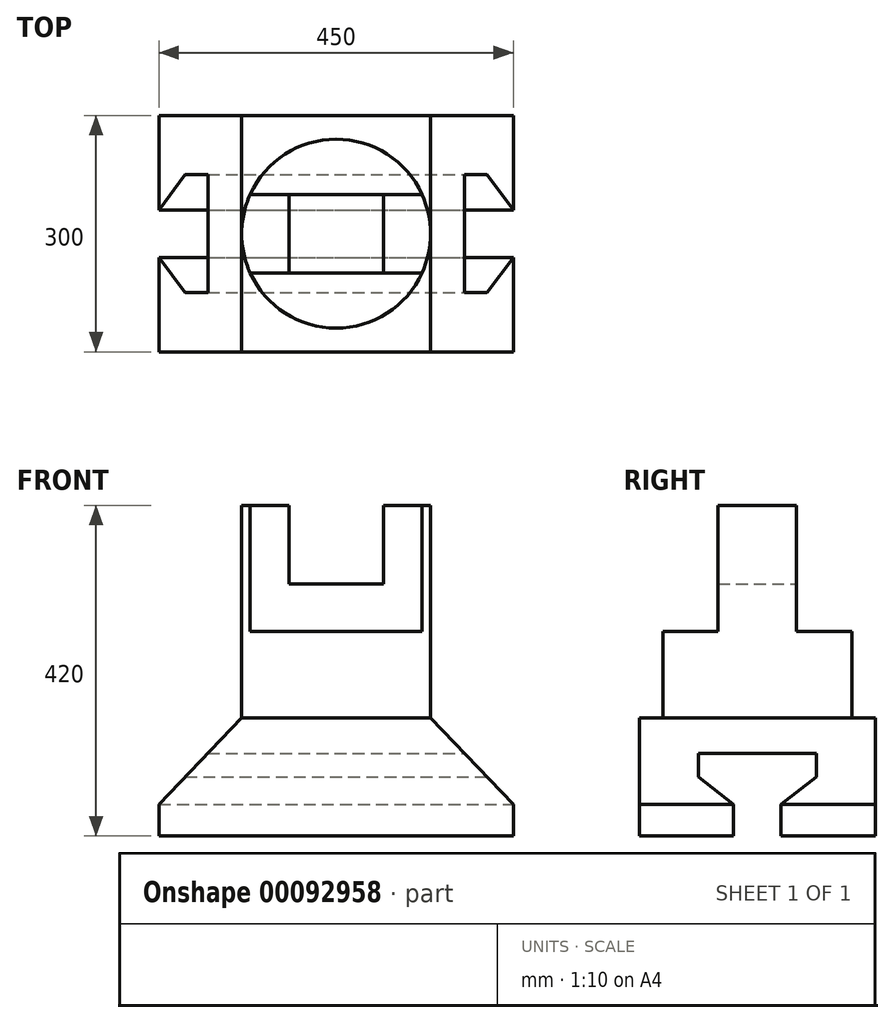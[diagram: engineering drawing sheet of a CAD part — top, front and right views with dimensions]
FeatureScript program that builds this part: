
annotation { "Feature Type Name" : "Feature", "Feature Type Description" : "" }
export const myFeature = defineFeature(function(context is Context, id is Id, definition is map)
    precondition{}
    {
        {
            var Q0;
            Q0=qCreatedBy(makeId("Front.planeOp"),FACE);
            var sketch = newSketch(context, id + "F0", { "sketchPlane" : qUnion([Q0])});
            skLineSegment(sketch, "E0.bottom", {"start": v(225, -75) * mm, "end": v(-225, -75) * mm});
            skLineSegment(sketch, "E0.top", {"start": v(120, 75) * mm, "end": v(-120, 75) * mm});
            skLineSegment(sketch, "E0.left", {"start": v(225, -75) * mm, "end": v(225, -35) * mm});
            skLineSegment(sketch, "E0.right", {"start": v(-225, -75) * mm, "end": v(-225, -35) * mm});
            skPoint(sketch, "E0.middle", {"position": v(0, 0) * mm});
            skLineSegment(sketch, "E1", {"start": v(-225, -35) * mm, "end": v(-120, 75) * mm});
            skLineSegment(sketch, "E2", {"start": v(120, 75) * mm, "end": v(225, -35) * mm});
            skPoint(sketch, "E3.orphan", {"position": v(-225, 75) * mm});
            skPoint(sketch, "E4.orphan", {"position": v(225, 75) * mm});
            skSolve(sketch);
        }
        {
            var Q0;
            Q0 = qSketchRegion(id + "F0", true);
            extrude(context, id + "F1", {"entities" : qUnion([Q0]), "endBound" : BoundingType.SYMMETRIC, "depth" : 300 * mm});
        }
        {
            var Q0;
            Q0=makeQuery(id+"F1.opExtrude","SWEPT_FACE",FACE,{"disambiguationData":[OSD([sQuery(id+"F0.wireOp",EDGE,"E0.top")])]});
            var sketch = newSketch(context, id + "F2", { "sketchPlane" : qUnion([Q0])});
            skCircle(sketch, "E5", {"center": v(0, 0) * mm, "radius": 120 * mm});
            skSolve(sketch);
        }
        {
            var Q0;
            Q0 = qSketchRegion(id + "F2", true);
            extrude(context, id + "F3", {"entities" : qUnion([Q0]), "operationType" : NewBodyOperationType.ADD, "depth" : 270 * mm});
        }
        {
            var Q0;
            Q0=makeQuery(id+"F3.opExtrude","CAP_FACE",FACE,{"disambiguationData":[OSD([sQuery(id+"F2.wireOp",EDGE,"E5")])],"isStart":false});
            var sketch = newSketch(context, id + "F4", { "sketchPlane" : qUnion([Q0])});
            skLineSegment(sketch, "E6.bottom", {"start": v(358.65, 50) * mm, "end": v(-358.65, 50) * mm});
            skLineSegment(sketch, "E6.top", {"start": v(358.65, -50) * mm, "end": v(-358.65, -50) * mm});
            skPoint(sketch, "E6.middle", {"position": v(0, 0) * mm});
            skLineSegment(sketch, "E7.bottom", {"start": v(-358.65, 50) * mm, "end": v(358.65, 50) * mm});
            skLineSegment(sketch, "E7.top", {"start": v(-358.65, 161.25) * mm, "end": v(358.65, 161.25) * mm});
            skLineSegment(sketch, "E7.left", {"start": v(-358.65, 50) * mm, "end": v(-358.65, 161.25) * mm});
            skLineSegment(sketch, "E7.right", {"start": v(358.65, 50) * mm, "end": v(358.65, 161.25) * mm});
            skLineSegment(sketch, "E8.bottom", {"start": v(358.65, -50) * mm, "end": v(-338.67, -50) * mm});
            skLineSegment(sketch, "E8.top", {"start": v(358.65, -198.35) * mm, "end": v(-338.67, -198.35) * mm});
            skLineSegment(sketch, "E8.left", {"start": v(358.65, -50) * mm, "end": v(358.65, -198.35) * mm});
            skLineSegment(sketch, "E8.right", {"start": v(-338.67, -50) * mm, "end": v(-338.67, -198.35) * mm});
            skSolve(sketch);
        }
        {
            var Q0;
            Q0 = qSketchRegion(id + "F4", true);
            extrude(context, id + "F5", {"entities" : qUnion([Q0]), "operationType" : NewBodyOperationType.REMOVE, "oppositeDirection" : true, "depth" : 160 * mm});
        }
        {
            var Q0;
            Q0=makeQuery(id+"F3.opExtrude","CAP_FACE",FACE,{"disambiguationData":[OSD([sQuery(id+"F2.wireOp",EDGE,"E5")])],"isStart":false});
            var sketch = newSketch(context, id + "F6", { "sketchPlane" : qUnion([Q0])});
            skLineSegment(sketch, "E9.bottom", {"start": v(60, -50) * mm, "end": v(-60, -50) * mm});
            skLineSegment(sketch, "E9.top", {"start": v(60, 50) * mm, "end": v(-60, 50) * mm});
            skLineSegment(sketch, "E9.left", {"start": v(60, -50) * mm, "end": v(60, 50) * mm});
            skLineSegment(sketch, "E9.right", {"start": v(-60, -50) * mm, "end": v(-60, 50) * mm});
            skPoint(sketch, "E9.middle", {"position": v(0, 0) * mm});
            skSolve(sketch);
        }
        {
            var Q0;
            Q0 = qSketchRegion(id + "F6", true);
            extrude(context, id + "F7", {"entities" : qUnion([Q0]), "operationType" : NewBodyOperationType.REMOVE, "oppositeDirection" : true, "depth" : 100 * mm});
        }
        {
            var Q0;
            Q0=makeQuery(id+"F1.opExtrude","SWEPT_FACE",FACE,{"disambiguationData":[OSD([sQuery(id+"F0.wireOp",EDGE,"E0.left")])]});
            var sketch = newSketch(context, id + "F8", { "sketchPlane" : qUnion([Q0])});
            skLineSegment(sketch, "E10", {"start": v(-30, -75) * mm, "end": v(-30, -35) * mm});
            skLineSegment(sketch, "E11", {"start": v(-30, -35) * mm, "end": v(-75, 0) * mm});
            skLineSegment(sketch, "E12", {"start": v(-75, 0) * mm, "end": v(-75, 30) * mm});
            skLineSegment(sketch, "E13", {"start": v(-75, 30) * mm, "end": v(75, 30) * mm});
            skLineSegment(sketch, "E14", {"start": v(75, 30) * mm, "end": v(75, 0) * mm});
            skLineSegment(sketch, "E15", {"start": v(75, 0) * mm, "end": v(30, -35) * mm});
            skLineSegment(sketch, "E16", {"start": v(30, -35) * mm, "end": v(30, -75) * mm});
            skLineSegment(sketch, "E17", {"start": v(30, -75) * mm, "end": v(-30, -75) * mm});
            skPoint(sketch, "E18", {"position": v(0, -75) * mm});
            skPoint(sketch, "E19", {"position": v(0, 30) * mm});
            skSolve(sketch);
        }
        {
            var Q0;
            Q0 = qSketchRegion(id + "F8", true);
            extrude(context, id + "F9", {"entities" : qUnion([Q0]), "operationType" : NewBodyOperationType.REMOVE, "endBound" : BoundingType.THROUGH_ALL, "oppositeDirection" : true, "depth" : 25 * mm});
        }
    });
